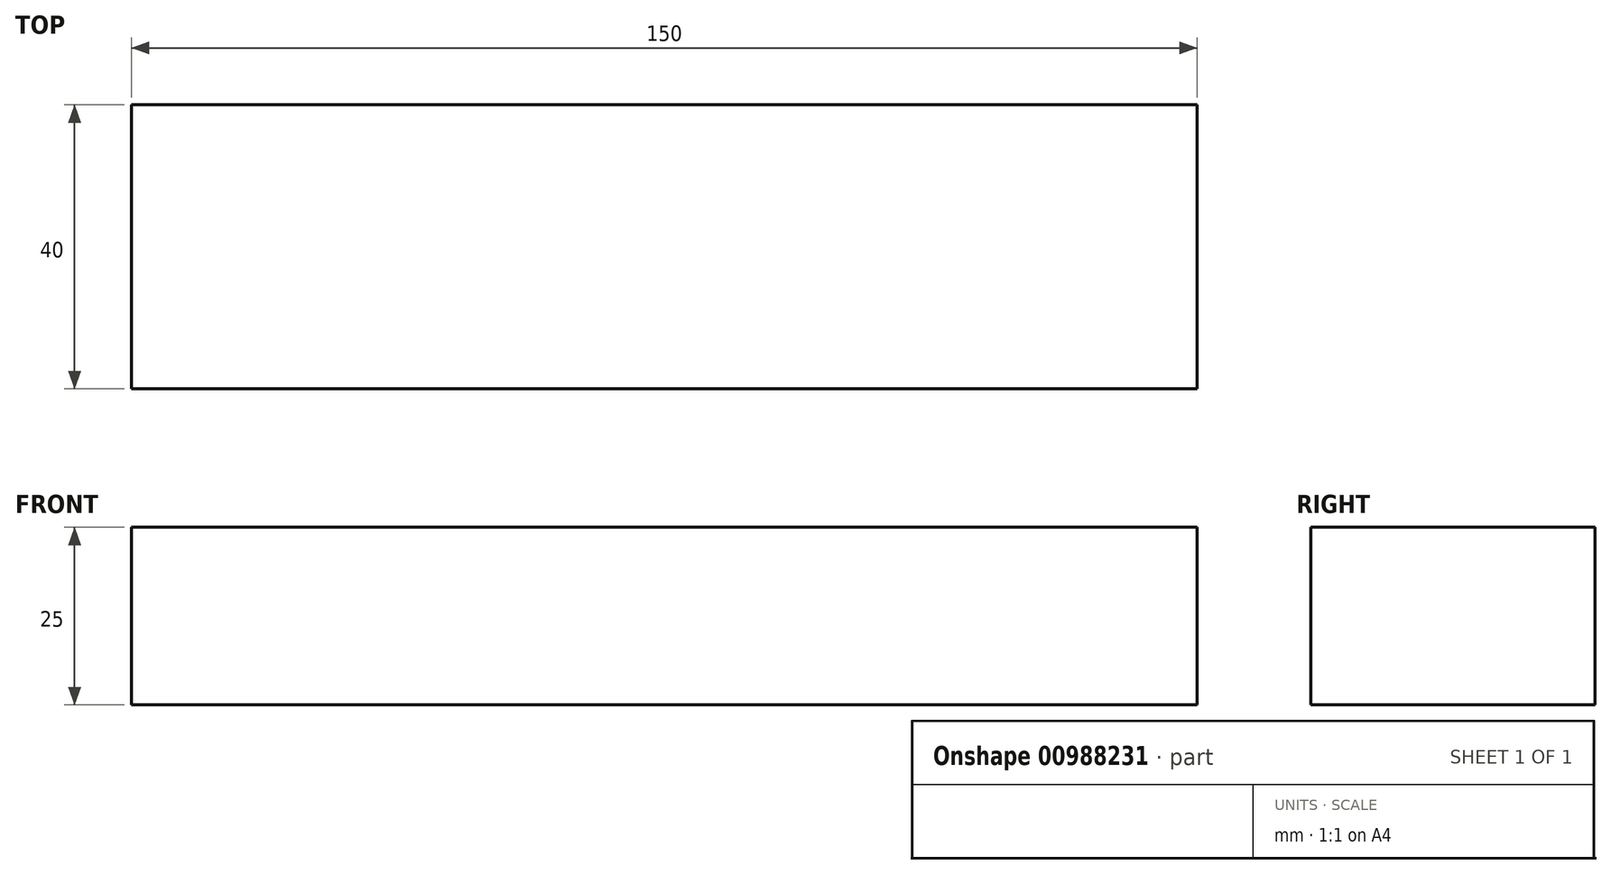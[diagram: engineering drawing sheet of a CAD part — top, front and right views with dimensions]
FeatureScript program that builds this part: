
annotation { "Feature Type Name" : "Feature", "Feature Type Description" : "" }
export const myFeature = defineFeature(function(context is Context, id is Id, definition is map)
    precondition{}
    {
        {
            var Q0;
            Q0=qCreatedBy(makeId("Top.planeOp"),FACE);
            var sketch = newSketch(context, id + "F0", { "sketchPlane" : qUnion([Q0])});
            skLineSegment(sketch, "E0.bottom", {"start": v(-66.83, 17.85) * mm, "end": v(83.17, 17.85) * mm});
            skLineSegment(sketch, "E0.top", {"start": v(-66.83, -22.15) * mm, "end": v(83.17, -22.15) * mm});
            skLineSegment(sketch, "E0.left", {"start": v(-66.83, 17.85) * mm, "end": v(-66.83, -22.15) * mm});
            skLineSegment(sketch, "E0.right", {"start": v(83.17, 17.85) * mm, "end": v(83.17, -22.15) * mm});
            skSolve(sketch);
        }
        {
            var Q0;
            Q0 = qSketchRegion(id + "F0", true);
            extrude(context, id + "F1", {"entities" : qUnion([Q0]), "depth" : 25 * mm, "offsetDistance" : 25 * mm});
        }
    });
